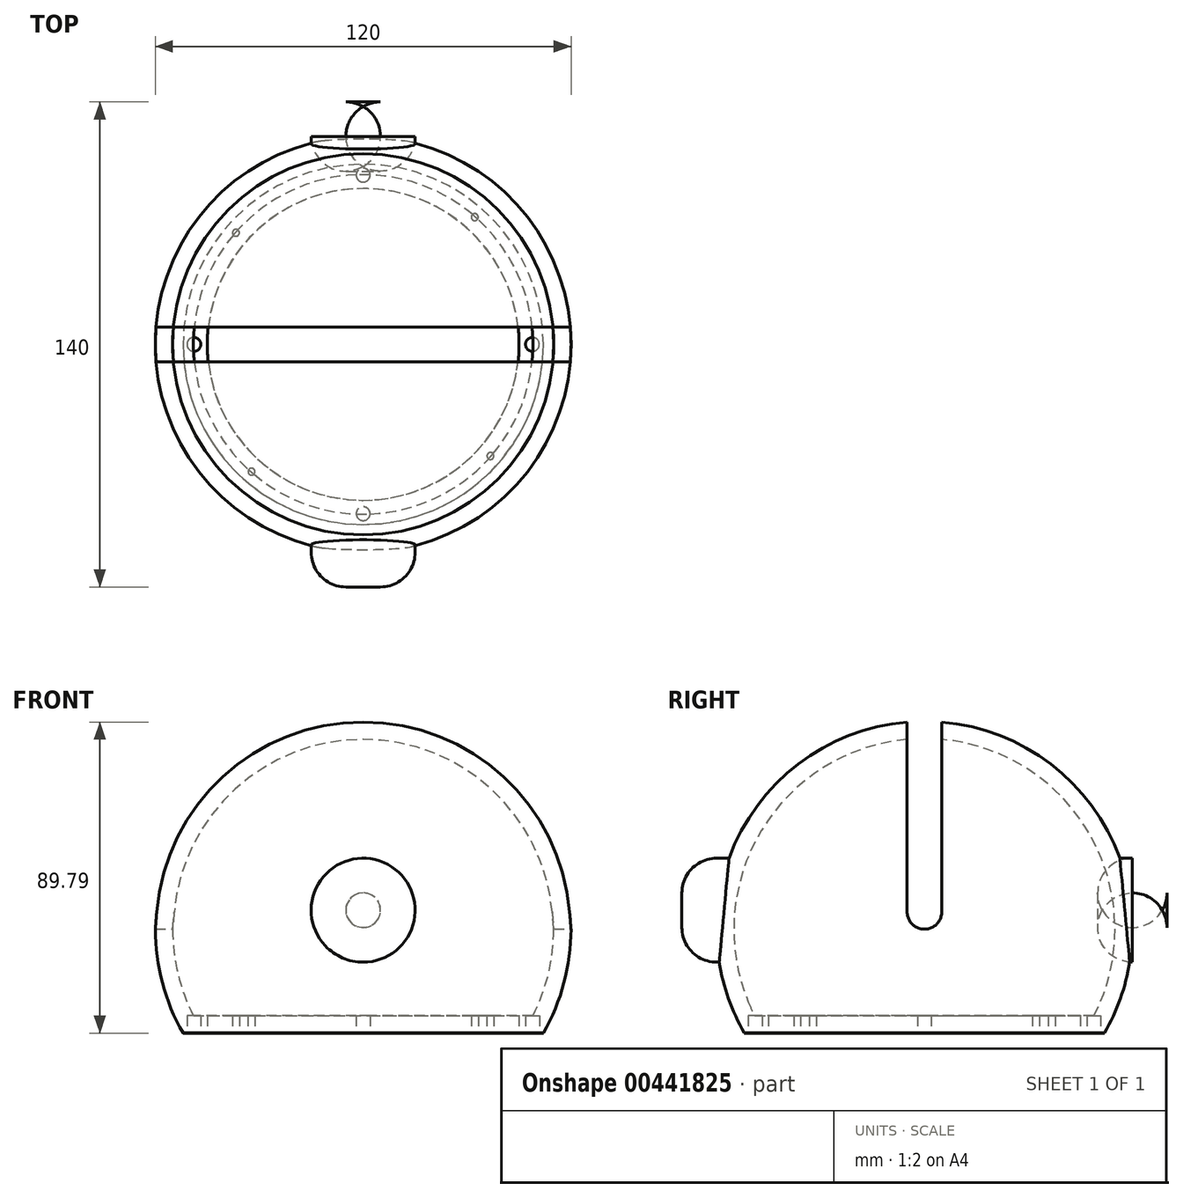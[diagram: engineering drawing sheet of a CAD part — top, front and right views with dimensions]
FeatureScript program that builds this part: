
annotation { "Feature Type Name" : "Feature", "Feature Type Description" : "" }
export const myFeature = defineFeature(function(context is Context, id is Id, definition is map)
    precondition{}
    {
        {
            var Q0;
            Q0=qCreatedBy(makeId("Top.planeOp"),FACE);
            var sketch = newSketch(context, id + "F0", { "sketchPlane" : qUnion([Q0])});
            skArc(sketch, "E0", {"start": v(60, 0) * mm, "mid": v(0, 60) * mm, "end": v(-60, 0) * mm});
            skArc(sketch, "E1.0", {"start": v(55, 0) * mm, "mid": v(0, 55) * mm, "end": v(-55, 0) * mm});
            skLineSegment(sketch, "E2", {"start": v(-60, 0) * mm, "end": v(-55, 0) * mm});
            skLineSegment(sketch, "E3.trimOffspring", {"start": v(55, 0) * mm, "end": v(60, 0) * mm});
            skLineSegment(sketch, "E4", {"start": v(-17.01, 0) * mm, "end": v(18, 0) * mm, "construction": true});
            skSolve(sketch);
        }
        {
            var Q0;
            Q0=makeQuery(id+"F0.imprint","IMPRINT",FACE,{"disambiguationData":[TD([[makeQuery(id+"F0.imprint","IMPRINT",EDGE,{"derivedFrom":sQuery(id+"F0.wireOp",EDGE,"E0")}),1.0]])]});
            var Q1;
            Q1=qConstructionFilter(qBodyType(qCreatedBy(id+"F0",EDGE),BodyType.WIRE),ConstructionObject.NO);
            var Q2;
            Q2=sQuery(id+"F0.wireOp",EDGE,"E4");
            revolve(context, id + "F1", {"entities" : qUnion([Q0]), "surfaceEntities" : qUnion([Q1]), "axis" : qUnion([Q2]), "revolveType" : RevolveType.FULL});
        }
        {
            var Q0;
            Q0=qCreatedBy(makeId("Top.planeOp"),FACE);
            cPlane(context, id + "F2", {"entities" : qUnion([Q0]), "cplaneType" : CPlaneType.OFFSET, "offset" : 30 * mm, "oppositeDirection" : true, "width" : 150 * mm, "height" : 150 * mm});
        }
        {
            var Q0;
            Q0=qCreatedBy(id+"F2.planeOp",FACE);
            var sketch = newSketch(context, id + "F3", { "sketchPlane" : qUnion([Q0])});
            skCircle(sketch, "E5", {"center": v(0, 0) * mm, "radius": 100 * mm});
            skCircle(sketch, "E6", {"center": v(0, 0) * mm, "radius": 50 * mm, "construction": true});
            skSolve(sketch);
        }
        {
            var Q0;
            Q0=qSketchRegion(id+"F3",true);
            extrude(context, id + "F4", {"entities" : qUnion([Q0]), "operationType" : NewBodyOperationType.REMOVE, "oppositeDirection" : true, "depth" : 40 * mm});
        }
        {
            var Q0;
            Q0=qCreatedBy(makeId("Right.planeOp"),FACE);
            var sketch = newSketch(context, id + "F5", { "sketchPlane" : qUnion([Q0])});
            skLineSegment(sketch, "E7.bottom", {"start": v(0, 68.9) * mm, "end": v(5, 68.9) * mm});
            skLineSegment(sketch, "E7.top", {"start": v(0, 0) * mm, "end": v(5, 0) * mm});
            skLineSegment(sketch, "E7.left", {"start": v(0, 68.9) * mm, "end": v(0, 0) * mm, "construction": true});
            skLineSegment(sketch, "E7.right", {"start": v(5, 68.9) * mm, "end": v(5, 0) * mm});
            skLineSegment(sketch, "E8.MirrorCS", {"start": v(0, 68.9) * mm, "end": v(-5, 68.9) * mm});
            skLineSegment(sketch, "E9.MirrorCS", {"start": v(-5, 68.9) * mm, "end": v(-5, 0) * mm});
            skLineSegment(sketch, "E10.MirrorCS", {"start": v(0, 0) * mm, "end": v(-5, 0) * mm});
            skSolve(sketch);
        }
        {
            var Q0;
            Q0=qSketchRegion(id+"F5",true);
            extrude(context, id + "F6", {"entities" : qUnion([Q0]), "operationType" : NewBodyOperationType.REMOVE, "oppositeDirection" : true, "depth" : 79.1 * mm, "hasSecondDirection" : true, "secondDirectionOppositeDirection" : false, "secondDirectionDepth" : 91.5 * mm});
        }
        {
            var Q0;
            Q0=makeQuery(id+"F6.boolean.opBoolean","COPY",EDGE,{"disambiguationData":[OD(1.0)],"derivedFrom":makeQuery(id+"F6.opExtrude","SWEPT_EDGE",EDGE,{"disambiguationData":[OSD([sQuery(id+"F5.wireOp",EDGE,"E9.MirrorCS"),sQuery(id+"F5.wireOp",EDGE,"E10.MirrorCS")])]})});
            var Q1;
            Q1=makeQuery(id+"F6.boolean.opBoolean","COPY",EDGE,{"disambiguationData":[OD(1.0)],"derivedFrom":makeQuery(id+"F6.opExtrude","SWEPT_EDGE",EDGE,{"disambiguationData":[OSD([sQuery(id+"F5.wireOp",EDGE,"E7.top"),sQuery(id+"F5.wireOp",EDGE,"E7.right")])]})});
            var Q2;
            Q2=makeQuery(id+"F6.boolean.opBoolean","COPY",EDGE,{"disambiguationData":[OD(0.0)],"derivedFrom":makeQuery(id+"F6.opExtrude","SWEPT_EDGE",EDGE,{"disambiguationData":[OSD([sQuery(id+"F5.wireOp",EDGE,"E9.MirrorCS"),sQuery(id+"F5.wireOp",EDGE,"E10.MirrorCS")])]})});
            var Q3;
            Q3=makeQuery(id+"F6.boolean.opBoolean","COPY",EDGE,{"disambiguationData":[OD(0.0)],"derivedFrom":makeQuery(id+"F6.opExtrude","SWEPT_EDGE",EDGE,{"disambiguationData":[OSD([sQuery(id+"F5.wireOp",EDGE,"E7.top"),sQuery(id+"F5.wireOp",EDGE,"E7.right")])]})});
            fillet(context, id + "F7", {"entities" : qUnion([Q0, Q1, Q2, Q3]), "radius" : 5 * mm, "tangentPropagation" : true, "allowEdgeOverflow" : false});
        }
        {
            var Q0;
            Q0=qCreatedBy(makeId("Front.planeOp"),FACE);
            var sketch = newSketch(context, id + "F8", { "sketchPlane" : qUnion([Q0])});
            skCircle(sketch, "E11", {"center": v(0, 5.48) * mm, "radius": 15 * mm});
            skSolve(sketch);
        }
        {
            var Q0;
            Q0=qSketchRegion(id+"F8",true);
            extrude(context, id + "F9", {"entities" : qUnion([Q0]), "operationType" : NewBodyOperationType.ADD, "depth" : 70 * mm, "hasSecondDirection" : true, "secondDirectionOppositeDirection" : true, "secondDirectionDepth" : 70 * mm});
        }
        {
            var Q0;
            Q0=makeQuery(id+"F9.opExtrude","CAP_EDGE",EDGE,{"disambiguationData":[OSD([sQuery(id+"F8.wireOp",EDGE,"E11")])],"isStart":false});
            var Q1;
            Q1=makeQuery(id+"F9.opExtrude","CAP_EDGE",EDGE,{"disambiguationData":[OSD([sQuery(id+"F8.wireOp",EDGE,"E11")])],"isStart":true});
            fillet(context, id + "F10", {"entities" : qUnion([Q0, Q1]), "radius" : 10 * mm, "tangentPropagation" : true, "allowEdgeOverflow" : false});
        }
        {
            var Q0;
            Q0=qCreatedBy(makeId("Top.planeOp"),FACE);
            var sketch = newSketch(context, id + "F11", { "sketchPlane" : qUnion([Q0])});
            skArc(sketch, "E12.0", {"start": v(55, 0) * mm, "mid": v(0, 55) * mm, "end": v(-55, 0) * mm});
            skLineSegment(sketch, "E13", {"start": v(55, 0) * mm, "end": v(-55, 0) * mm});
            skSolve(sketch);
        }
        {
            var Q0;
            Q0=qSketchRegion(id+"F11",true);
            var Q1;
            Q1=sQuery(id+"F11.wireOp",EDGE,"E13");
            revolve(context, id + "F12", {"operationType" : NewBodyOperationType.REMOVE, "entities" : qUnion([Q0]), "axis" : qUnion([Q1]), "revolveType" : RevolveType.FULL, "oppositeDirection" : true});
        }
        {
            var Q0;
            Q0=makeQuery(id+"F4.boolean.opBoolean","COPY",FACE,{"derivedFrom":makeQuery(id+"F4.opExtrude","CAP_FACE",FACE,{"disambiguationData":[OSD([sQuery(id+"F3.wireOp",EDGE,"E5")])],"isStart":true})});
            var sketch = newSketch(context, id + "F13", { "sketchPlane" : qUnion([Q0])});
            skCircle(sketch, "E14", {"center": v(0, 0) * mm, "radius": 45 * mm});
            skCircle(sketch, "E15", {"center": v(0, 0) * mm, "radius": 52 * mm});
            skSolve(sketch);
        }
        {
            var Q0;
            Q0 = qSketchRegion(id + "F13", true);
            extrude(context, id + "F14", {"entities" : qUnion([Q0]), "operationType" : NewBodyOperationType.ADD, "oppositeDirection" : true, "depth" : 5 * mm});
        }
        {
            var Q0;
            Q0=makeQuery(id+"F14.boolean.opBoolean","MERGE",FACE,{"derivedFrom":[makeQuery(id+"F4.boolean.opBoolean","COPY",FACE,{"derivedFrom":makeQuery(id+"F4.opExtrude","CAP_FACE",FACE,{"disambiguationData":[OSD([sQuery(id+"F3.wireOp",EDGE,"E5")])],"isStart":true})}),makeQuery(id+"F14.opExtrude","CAP_FACE",FACE,{"disambiguationData":[OSD([sQuery(id+"F13.wireOp",EDGE,"E14"),sQuery(id+"F13.wireOp",EDGE,"E15")])],"isStart":true})]});
            var sketch = newSketch(context, id + "F15", { "sketchPlane" : qUnion([Q0])});
            skCircle(sketch, "E16", {"center": v(0, 0) * mm, "radius": 48.86 * mm, "construction": true});
            skCircle(sketch, "E17", {"center": v(48.86, 0) * mm, "radius": 2 * mm});
            skCircle(sketch, "E18", {"center": v(36.73, 32.22) * mm, "radius": 1 * mm});
            skCircle(sketch, "E19.1.0", {"center": v(-32.22, 36.73) * mm, "radius": 1 * mm});
            skCircle(sketch, "E19.1.1", {"center": v(0, 48.86) * mm, "radius": 2 * mm});
            skCircle(sketch, "E19.2.0", {"center": v(-36.73, -32.22) * mm, "radius": 1 * mm});
            skCircle(sketch, "E19.2.1", {"center": v(-48.86, 0) * mm, "radius": 2 * mm});
            skCircle(sketch, "E19.3.0", {"center": v(32.22, -36.73) * mm, "radius": 1 * mm});
            skCircle(sketch, "E19.3.1", {"center": v(0, -48.86) * mm, "radius": 2 * mm});
            skSolve(sketch);
        }
        {
            var Q0;
            Q0 = qSketchRegion(id + "F15", true);
            extrude(context, id + "F16", {"entities" : qUnion([Q0]), "operationType" : NewBodyOperationType.REMOVE, "oppositeDirection" : true, "depth" : 5 * mm});
        }
    });
